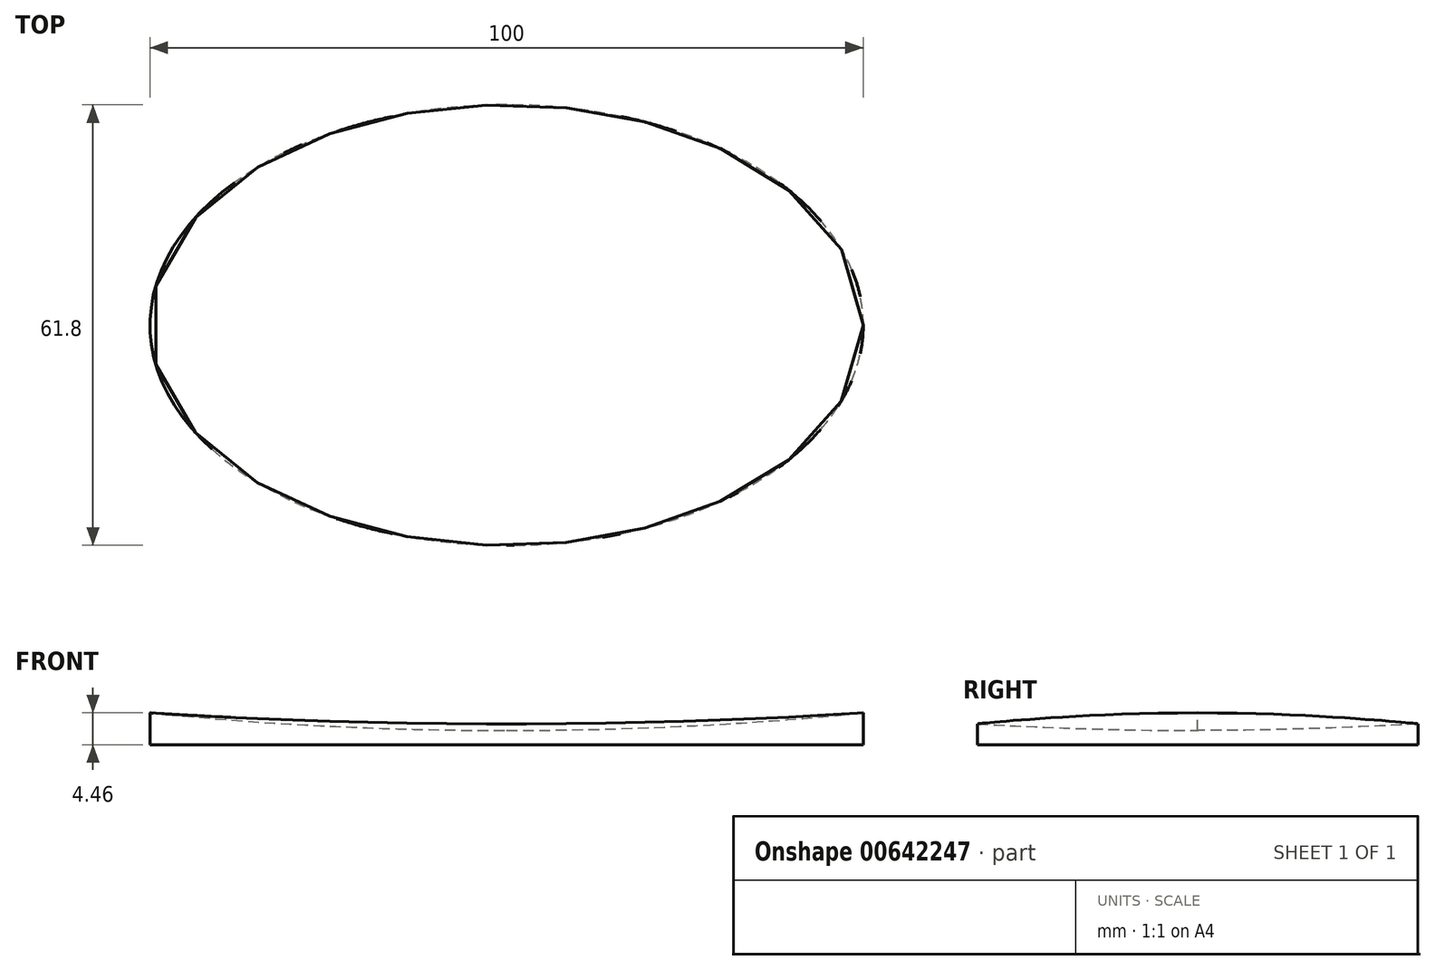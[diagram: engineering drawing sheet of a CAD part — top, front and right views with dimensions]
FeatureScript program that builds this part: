
annotation { "Feature Type Name" : "Feature", "Feature Type Description" : "" }
export const myFeature = defineFeature(function(context is Context, id is Id, definition is map)
    precondition{}
    {
        {
            var Q0;
            Q0=qCreatedBy(makeId("Top.planeOp"),FACE);
            var sketch = newSketch(context, id + "F0", { "sketchPlane" : qUnion([Q0])});
            skEllipse(sketch, "E0", {"center": v(0, 0) * mm, "majorRadius": 50 * mm, "minorRadius": 30.9 * mm, "majorAxis": v(1, 0)});
            skEllipticalArc(sketch, "E1.0.1.0", {});
            skEllipticalArc(sketch, "E1.0.2.0", {});
            skEllipticalArc(sketch, "E1.0.3.0", {});
            skEllipticalArc(sketch, "E1.0.4.0", {});
            skEllipticalArc(sketch, "E1.0.5.0", {});
            skEllipticalArc(sketch, "E1.0.6.0", {});
            skEllipticalArc(sketch, "E1.0.7.0", {});
            skEllipticalArc(sketch, "E1.0.8.0", {});
            skEllipticalArc(sketch, "E1.0.9.0", {});
            skEllipticalArc(sketch, "E1.0.10.0", {});
            skEllipticalArc(sketch, "E1.0.11.0", {});
            skEllipticalArc(sketch, "E1.0.12.0", {});
            skEllipticalArc(sketch, "E1.0.13.0", {});
            skEllipticalArc(sketch, "E1.0.14.0", {});
            skEllipticalArc(sketch, "E1.0.15.0", {});
            skEllipticalArc(sketch, "E1.0.16.0", {});
            skEllipticalArc(sketch, "E1.0.17.0", {});
            skLineSegment(sketch, "E1.direction1", {"start": v(-142.93, 28.69) * mm, "end": v(-117.93, 28.69) * mm, "construction": true});
            skLineSegment(sketch, "E1.direction2", {"start": v(-142.93, 28.69) * mm, "end": v(-142.93, 33.69) * mm, "construction": true});
            skFitSpline(sketch, "E2.0", {"points": [v(54.95, -1.94) * mm, v(55.03, 0) * mm, v(54.95, 1.94) * mm, v(54.64, 4.49) * mm, v(53.88, 7.62) * mm, v(52.41, 11.22) * mm, v(50.43, 14.64) * mm, v(47.97, 17.86) * mm, v(45.07, 20.85) * mm, v(42.3, 23.15) * mm, v(39.9, 24.88) * mm, v(38, 26.11) * mm, v(36.01, 27.28) * mm, v(33.27, 28.74) * mm, v(29.68, 30.38) * mm, v(25.14, 32.06) * mm, v(20.4, 33.44) * mm, v(15.49, 34.53) * mm, v(10.43, 35.31) * mm, v(6.12, 35.71) * mm, v(2.64, 35.87) * mm, v(0, 35.91) * mm, v(-2.64, 35.87) * mm, v(-6.12, 35.71) * mm, v(-10.43, 35.31) * mm, v(-15.49, 34.53) * mm, v(-20.4, 33.44) * mm, v(-25.14, 32.06) * mm, v(-29.68, 30.38) * mm, v(-33.27, 28.74) * mm, v(-36.01, 27.28) * mm, v(-38, 26.11) * mm, v(-39.9, 24.88) * mm, v(-42.3, 23.15) * mm, v(-45.07, 20.85) * mm, v(-47.97, 17.86) * mm, v(-50.43, 14.64) * mm, v(-52.41, 11.22) * mm, v(-53.88, 7.62) * mm, v(-54.64, 4.49) * mm, v(-54.95, 1.94) * mm, v(-55.03, 0) * mm, v(-54.95, -1.94) * mm, v(-54.64, -4.49) * mm, v(-53.88, -7.62) * mm, v(-52.41, -11.22) * mm, v(-50.43, -14.64) * mm, v(-47.97, -17.86) * mm, v(-45.07, -20.85) * mm, v(-42.3, -23.15) * mm, v(-39.9, -24.88) * mm, v(-38, -26.11) * mm, v(-36.01, -27.28) * mm, v(-33.27, -28.74) * mm, v(-29.68, -30.38) * mm, v(-25.14, -32.06) * mm, v(-20.4, -33.44) * mm, v(-15.49, -34.53) * mm, v(-10.43, -35.31) * mm, v(-6.12, -35.71) * mm, v(-2.64, -35.87) * mm, v(0, -35.91) * mm, v(2.64, -35.87) * mm, v(6.12, -35.71) * mm, v(10.43, -35.31) * mm, v(15.49, -34.53) * mm, v(20.4, -33.44) * mm, v(25.14, -32.06) * mm, v(29.68, -30.38) * mm, v(33.27, -28.74) * mm, v(36.01, -27.28) * mm, v(38, -26.11) * mm, v(39.9, -24.88) * mm, v(42.3, -23.15) * mm, v(45.07, -20.85) * mm, v(47.97, -17.86) * mm, v(50.43, -14.64) * mm, v(52.41, -11.22) * mm, v(53.88, -7.62) * mm, v(54.64, -4.49) * mm, v(54.95, -1.94) * mm, v(55.03, 0) * mm, v(54.95, 1.94) * mm, v(54.95, -1.94) * mm]});
            const initialGuessF0  = {"E1.0.1.0": [-0.00973100278268231, 0.006642725386501749, -0.7071067811865475, -0.7071067811865476, 0.05020502209663391, 0.030644073124345944, 4.957398048638654, 5.471694386240636], "E1.0.2.0": [-0.006195468876749571, 0.0031071914805690173, -0.7071067811865475, -0.7071067811865476, 0.05020502209663391, 0.030644073124345944, 4.66981387009846, 5.581585844402488], "E1.0.3.0": [-0.002659934970816503, -0.00042834242536543554, -0.7071067811865475, -0.7071067811865476, 0.05020502209663391, 0.030644073124345944, 4.455273301651485, 5.611954590165249], "E1.0.4.0": [0.0008755989351159066, -0.003963876331296461, -0.7071067811865475, -0.7071067811865476, 0.05020502209663391, 0.030644073124345944, 4.2696489326466835, 5.610110772737695], "E1.0.5.0": [0.0044111328410486456, -0.0074994102372292, -0.7071067811865475, -0.7071067811865476, 0.05020502209663391, 0.030644073124345944, 4.102459779734023, 5.589924699953796], "E1.0.6.0": [0.007946666746981385, -0.011034944143161939, -0.7071067811865475, -0.7071067811865476, 0.05020502209663391, 0.030644073124345944, 3.952495873774472, 5.557714491834231], "E1.0.7.0": [0.011482200652914124, -0.01457047804909467, -0.7071067811865475, -0.7071067811865476, 0.05020502209663391, 0.030644073124345944, 3.8248758058846626, 5.51681181291913], "E1.0.8.0": [0.015017734558846849, -0.01810601195502741, -0.7071067811865475, -0.7071067811865476, 0.05020502209663391, 0.030644073124345944, 3.7290779145467585, 5.46905499745489], "E1.0.9.0": [0.0185532684647796, -0.02164154586096015, -0.7071067811865475, -0.7071067811865476, 0.05020502209663391, 0.030644073124345944, 3.672612489113611, 5.41541178571194], "E1.0.10.0": [0.02208880237071234, -0.025177079766892894, -0.7071067811865475, -0.7071067811865476, 0.05020502209663391, 0.030644073124345944, 3.6544811455315274, 5.356261888708082], "E1.0.11.0": [0.02562433627664508, -0.028712613672825626, -0.7071067811865475, -0.7071067811865476, 0.05020502209663391, 0.030644073124345944, 3.667270373283357, 5.291508427136841], "E1.0.12.0": [0.029159870182577804, -0.032248147578758365, -0.7071067811865475, -0.7071067811865476, 0.05020502209663391, 0.030644073124345944, 3.7033601545527652, 5.220569002820531], "E1.0.13.0": [0.03269540408851056, -0.035783681484691104, -0.7071067811865475, -0.7071067811865476, 0.05020502209663391, 0.030644073124345944, 3.7579117296538995, 5.142228684083149], "E1.0.14.0": [0.03623093799444328, -0.03931921539062383, -0.7071067811865475, -0.7071067811865476, 0.05020502209663391, 0.030644073124345944, 3.829272709887173, 5.05423667237879], "E1.0.15.0": [0.03976647190037601, -0.04285474929655657, -0.7071067811865475, -0.7071067811865476, 0.05020502209663391, 0.030644073124345944, 3.919379688123939, 4.952224384494373], "E1.0.16.0": [0.04330200580630876, -0.04639028320248932, -0.7071067811865475, -0.7071067811865476, 0.05020502209663391, 0.030644073124345944, 4.03683889651958, 4.826060534885393], "E1.0.17.0": [0.04683753971224151, -0.04992581710842206, -0.7071067811865475, -0.7071067811865476, 0.05020502209663391, 0.030644073124345944, 4.219669900747702, 4.63674861435654]};
            skSetInitialGuess(sketch, initialGuessF0);
            skSolve(sketch);
        }
        {
            var Q0;
            Q0 = qSketchRegion(id + "F0", true);
            var Q1;
            {var subQ0=sQuery(id+"F0.wireOp",EDGE,"E1.0.1.0");Q1=makeQuery(id+"F0.imprint","IMPRINT",FACE,{"disambiguationData":[TD([[makeQuery(id+"F0.imprint","IMPRINT",EDGE,{"derivedFrom":subQ0}),1.0]])]});}
            var Q2;
            {var subQ0=sQuery(id+"F0.wireOp",EDGE,"E1.0.3.0");Q2=makeQuery(id+"F0.imprint","IMPRINT",FACE,{"disambiguationData":[TD([[makeQuery(id+"F0.imprint","IMPRINT",EDGE,{"derivedFrom":subQ0}),1.0]])]});}
            var Q3;
            {var subQ0=sQuery(id+"F0.wireOp",EDGE,"E1.0.5.0");Q3=makeQuery(id+"F0.imprint","IMPRINT",FACE,{"disambiguationData":[TD([[makeQuery(id+"F0.imprint","IMPRINT",EDGE,{"derivedFrom":subQ0}),1.0]])]});}
            var Q4;
            {var subQ0=sQuery(id+"F0.wireOp",EDGE,"E1.0.7.0");Q4=makeQuery(id+"F0.imprint","IMPRINT",FACE,{"disambiguationData":[TD([[makeQuery(id+"F0.imprint","IMPRINT",EDGE,{"derivedFrom":subQ0}),1.0]])]});}
            var Q5;
            {var subQ0=sQuery(id+"F0.wireOp",EDGE,"E1.0.9.0");Q5=makeQuery(id+"F0.imprint","IMPRINT",FACE,{"disambiguationData":[TD([[makeQuery(id+"F0.imprint","IMPRINT",EDGE,{"derivedFrom":subQ0}),1.0]])]});}
            var Q6;
            {var subQ0=sQuery(id+"F0.wireOp",EDGE,"E1.0.11.0");Q6=makeQuery(id+"F0.imprint","IMPRINT",FACE,{"disambiguationData":[TD([[makeQuery(id+"F0.imprint","IMPRINT",EDGE,{"derivedFrom":subQ0}),1.0]])]});}
            var Q7;
            {var subQ0=sQuery(id+"F0.wireOp",EDGE,"E1.0.13.0");Q7=makeQuery(id+"F0.imprint","IMPRINT",FACE,{"disambiguationData":[TD([[makeQuery(id+"F0.imprint","IMPRINT",EDGE,{"derivedFrom":subQ0}),1.0]])]});}
            var Q8;
            {var subQ0=sQuery(id+"F0.wireOp",EDGE,"E1.0.15.0");Q8=makeQuery(id+"F0.imprint","IMPRINT",FACE,{"disambiguationData":[TD([[makeQuery(id+"F0.imprint","IMPRINT",EDGE,{"derivedFrom":subQ0}),1.0]])]});}
            var Q9;
            {var subQ0=sQuery(id+"F0.wireOp",EDGE,"E1.0.17.0");Q9=makeQuery(id+"F0.imprint","IMPRINT",FACE,{"disambiguationData":[TD([[makeQuery(id+"F0.imprint","IMPRINT",EDGE,{"derivedFrom":subQ0}),1.0]])]});}
            extrude(context, id + "F1", {"entities" : qUnion([Q0, Q1, Q2, Q3, Q4, Q5, Q6, Q7, Q8, Q9]), "depth" : 25 * mm, "offsetDistance" : 25 * mm});
        }
        {
            var Q0;
            Q0=qCreatedBy(makeId("Front.planeOp"),FACE);
            var sketch = newSketch(context, id + "F2", { "sketchPlane" : qUnion([Q0])});
            skLineSegment(sketch, "E3", {"start": v(0, 0) * mm, "end": v(0, 2) * mm, "construction": true});
            skLineSegment(sketch, "E4", {"start": v(55.03, 0) * mm, "end": v(55.03, 5) * mm, "construction": true});
            skEllipticalArc(sketch, "E5", {});
            skLineSegment(sketch, "E6", {"start": v(0, 2) * mm, "end": v(0, 37.11) * mm});
            skLineSegment(sketch, "E7", {"start": v(0, 37.11) * mm, "end": v(127.58, 21.89) * mm});
            const initialGuessF2  = {"E5": [0, 0.04811422526836395, 0, -1, 0.04611422526836396, 0.1551012592859918, 6.283185307179586, 0.96586980753872]};
            skSetInitialGuess(sketch, initialGuessF2);
            skSolve(sketch);
        }
        {
            var Q0;
            Q0=qCreatedBy(makeId("Front.planeOp"),FACE);
            var sketch = newSketch(context, id + "F3", { "sketchPlane" : qUnion([Q0])});
            skLineSegment(sketch, "E8", {"start": v(0, 73.84) * mm, "end": v(0, -18.6) * mm, "construction": true});
            skSolve(sketch);
        }
        {
            var Q0;
            Q0=makeQuery(id+"F2.imprint","IMPRINT",FACE,{"disambiguationData":[TD([[makeQuery(id+"F2.imprint","IMPRINT",EDGE,{"derivedFrom":sQuery(id+"F2.wireOp",EDGE,"E5")}),1.0]])]});
            var Q1;
            Q1=sQuery(id+"F3.wireOp",EDGE,"E8");
            revolve(context, id + "F4", {"operationType" : NewBodyOperationType.REMOVE, "entities" : qUnion([Q0]), "axis" : qUnion([Q1]), "revolveType" : RevolveType.FULL, "oppositeDirection" : true});
        }
    });
